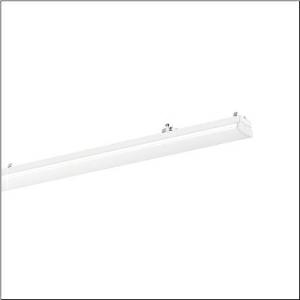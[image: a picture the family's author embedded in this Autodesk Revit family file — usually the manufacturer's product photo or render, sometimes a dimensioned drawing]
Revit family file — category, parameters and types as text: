
# Revit family: licross_r__11_recessed_opal_mo_51tl1d7n48xg_8506
name_source: partatom
category: Lighting Fixtures
units: mm (PartAtom-declared; Revit-internal decimal feet)

## family parameters
Cut with Voids When Loaded = No
Host = Face
Light Source = No
Part Type = Normal
Room Calculation Point = No
Round Connector Dimension = Use Diameter
Shared = No

## types (1)
- Licross® 11 recessed opal MO (1 x LED, 8490 lm, 48.5 W, 4000K)
    Apparent Load = 49 VA
    CIE Flux Codes = 44 73 91 87 100
    Color Rendering = 80
    Color Temperature = 4000K
    Default Elevation = 1800 mm
    Description = Licross® 11 recessed opal MO, luminaire insert, of sheet steel, coil coated, white, length: 1.500mm, width: 76mm, height: 87mm, LED rated luminous flux: 8.490lm, light colour: 840, control gear: ON/OFF, with plug, 3-pole, with phase selection, mains connection: 220..240V, AC, 50/60Hz, rated input power: 49W, internal wiring halogen-free, primary optical cover: cover, of PMMA, light emission: direct with ceiling illumination distribution, primary light characteristic: symmetric, protection rating (complete): IP40, insulation class (complete): insulation class I (protective earthing), certification: CE, ENEC, VDE, UKCA, protection symbol: D if used in an environment without relevant dust loads with corresponding accessories, impact resistance: IK06, permissible ambient temperature for indoor applications: -35..+35°C, corresponds to IFS (International Featured Standards) requirements for safety and quality in the food industry, reducing of maximum allowable ambient temperature of 5°C with ceiling mounting, packaging unit: 1 piece
    Height = 83 mm
    Lamp = 1 x LED
    Lamp Light Flux = 8490 lm
    Lamp Power = 48.5 W
    Lamp count = 1
    Length = 1500 mm
    Luminous efficacy = 175 lm/W
    Manufacturer = Siteco
    ModVariant = No
    Model = 51TL1D7N48XG
    Mounting Place = Ceiling
    Mounting Type = Pendant
    Number of Poles = 1
    OnlyDefault = Yes
    Power Factor = 1
    Product Name = Licross® 11 recessed opal MO
    Product group = luminaire insert | ceiling pendant
    ProductGroupID = 902
    Protection Class = Protection class I
    Protection Degree = IP 40
    RLX_Detail_Level = 1
    RLX_Emergency_Light_Flux = 0 lm
    RLX_Emergency_Type = 0
    RLX_Emergency_Type_DB = No
    RlxData = <blob elided: 23197 chars, md5=f149127d>
    Socket = socket
    Standby Power = 0 W
    System Light Flux = 8490 lm
    System Power = 49 W
    Type Comments = Product without accessories
    Type Image = l_1313666.jpg
    URL = http://relux.com
    VarID = ---
    Voltage = 0 V
    Weight = 0.00 kg
    Width = 76 mm

## geometry (parser evidence)
native form markers: Blend x4, Sweep x15
no freeform markers — native parametric forms only
